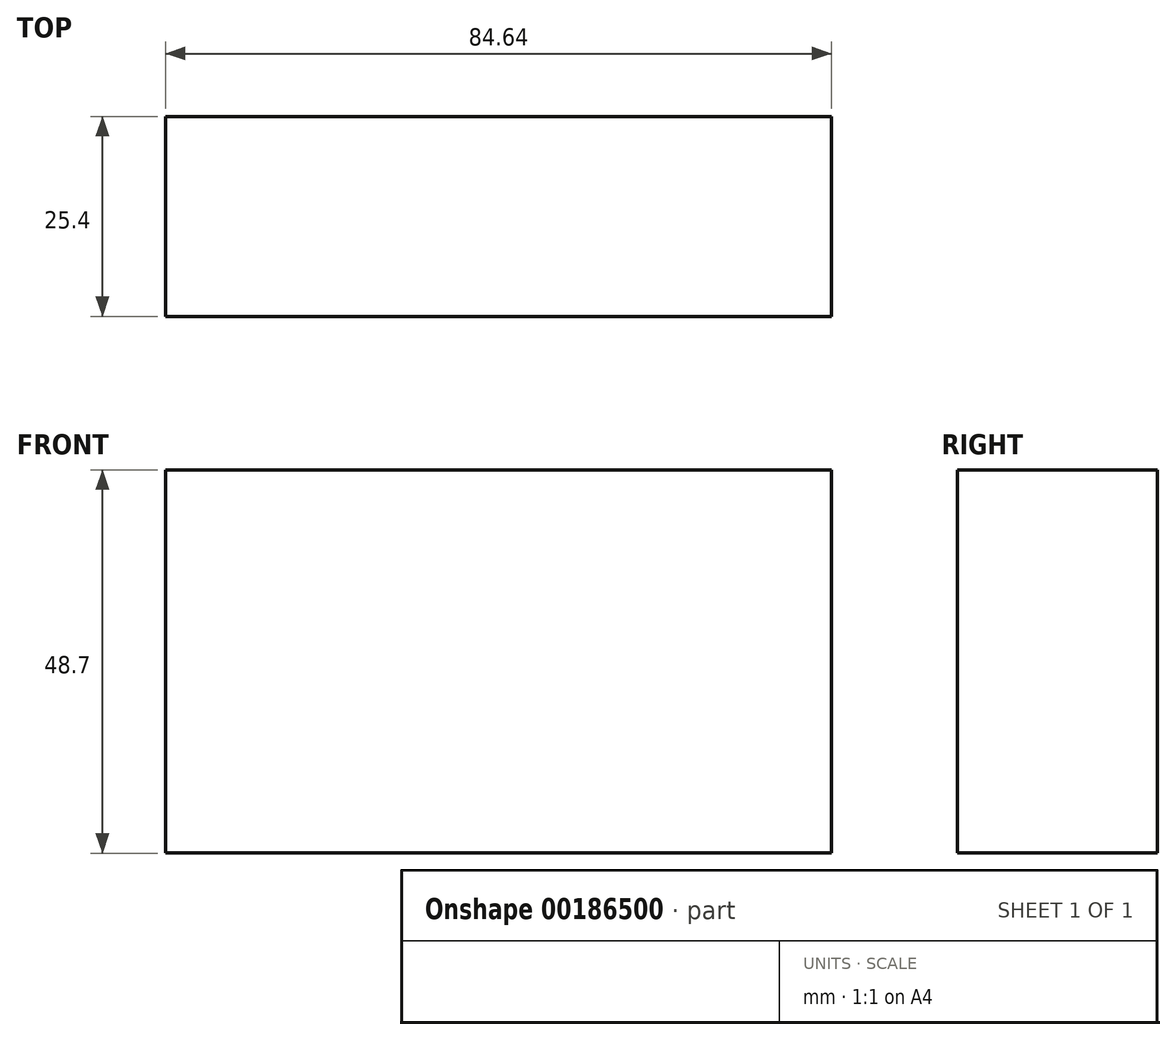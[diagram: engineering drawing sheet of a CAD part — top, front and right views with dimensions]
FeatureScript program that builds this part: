
annotation { "Feature Type Name" : "Feature", "Feature Type Description" : "" }
export const myFeature = defineFeature(function(context is Context, id is Id, definition is map)
    precondition{}
    {
        {
            var Q0;
            Q0=qCreatedBy(makeId("Front.planeOp"),FACE);
            var sketch = newSketch(context, id + "F0", { "sketchPlane" : qUnion([Q0])});
            skLineSegment(sketch, "E0.bottom", {"start": v(43.68, 25.35) * mm, "end": v(-40.96, 25.35) * mm});
            skLineSegment(sketch, "E0.top", {"start": v(43.68, -23.35) * mm, "end": v(-40.96, -23.35) * mm});
            skLineSegment(sketch, "E0.left", {"start": v(43.68, 25.35) * mm, "end": v(43.68, -23.35) * mm});
            skLineSegment(sketch, "E0.right", {"start": v(-40.96, 25.35) * mm, "end": v(-40.96, -23.35) * mm});
            skPoint(sketch, "E0.middle", {"position": v(1.36, 1) * mm});
            skSolve(sketch);
        }
        {
            var Q0;
            Q0 = qSketchRegion(id + "F0", true);
            extrude(context, id + "F1", {"entities" : qUnion([Q0]), "depth" : 25.4 * mm});
        }
    });
